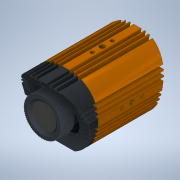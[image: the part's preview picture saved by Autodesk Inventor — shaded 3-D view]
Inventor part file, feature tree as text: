
AUTODESK INVENTOR PART (.ipt)
format: ipt  version: 2022 (Build 260153000, 153)  size: 11,512,320 bytes
history: native  units: mm
features: sketch x28, extrude x16, plane x8, hole x8, projected_geometry x6, other x3, chamfer x2, split x1, helix x1, pattern_circular x1, mirror x1
ambient origin geometry x8: Origin, YZ Plane, XZ Plane, XY Plane, X Axis, Y Axis, Z Axis, Center Point
bodies: Solid1 (feature_tree), Solid2 (feature_tree), Solid3 (feature_tree)
feature tree (75):
  extrude  "Extrusion1"  Depth=62.28mm
  extrude  "Extrusion2"  Depth=9.388mm
  sketch  "Sketch3"  dims[d5=18.0mm d6=31.8mm]
  plane  "Work Plane2"
  extrude  "Extrusion3"  Depth=31.8mm
  extrude  "Extrusion4"  Depth=14.0mm
  extrude  "Extrusion5"  Depth=94.6mm TaperAngle=0.0deg
  chamfer  "Chamfer1"  Distance=1.6mm Angle=90.0deg
  extrude  "Extrusion6"  Depth=94.6mm TaperAngle=0.0deg
  chamfer  "Chamfer2"  Distance=9.72mm
  hole  "Hole1"  [1 undecoded]
  hole  "Hole2"  [1 undecoded]
  hole  "Hole3"  [1 undecoded]
  hole  "Hole4"  [1 undecoded]
  hole  "Hole5"  [1 undecoded]
  hole  "Hole6"  [1 undecoded]
  hole  "Hole7"  [1 undecoded]
  hole  "Hole8"  [1 undecoded]
  plane  "Work Plane4"
  plane  "Work Plane5"
  plane  "Work Plane6"
  extrude  "Extrusion9"  Depth=8.0mm
  extrude  "Extrusion10"  Depth=40.0mm
  extrude  "Extrusion11"  Depth=32.5mm
  extrude  "Extrusion12"  Depth=25.0mm
  extrude  "Extrusion13"  Depth=32.5mm
  extrude  "Extrusion14"  Depth=10.0mm
  extrude  "Extrusion15"  Depth=4.3mm TaperAngle=0.0deg
  extrude  "Extrusion16"  TaperAngle=90.0deg  [1 undecoded]
  extrude  "Extrusion17"  Depth=10.0mm TaperAngle=0.0deg
  extrude  "Extrusion18"  Depth=50.8mm
  sketch  "Sketch30"  dims[d95=32.5mm]
  split  "Split1"
  helix  "Coil1"  [1 undecoded]
  pattern_circular  "Circular Pattern1"  [2 undecoded]
  plane  "Work Plane9"
  mirror  "Mirror1"
  plane  "Work Plane10"
  sketch  "Sketch35"  dims[d104=4.978mm d105=8.7mm d106=4.0mm d107=2.0mm d108=90.0deg d109=9.05mm d110=20.594885mm d111=4.3mm d119=0.0mm d125=90.0deg d132=10.0mm d133=0.0mm d135=50.8mm d136=6.97mm d137=4.86mm d139=7.7mm d140=3.15mm d141=3.15mm d142=1.12mm d143=1.12mm d144=3.15mm d145=1.12mm d146=3.15mm d147=3.15mm d148=1.12mm d149=3.15mm d151=7.7mm d152=3.15mm d153=1.12mm d154=3.15mm d155=1.12mm d156=3.15mm d157=3.15mm d158=1.12mm d159=3.15mm d160=1.12mm d161=3.15mm d162=10.0mm d163=0.0mm d164=13.86mm d165=0.0mm d166=0.8mm d167=1.6mm d168=2.27mm d169=0.0mm d172=0.82mm d173=0.3mm d175=0.3mm d176=0.3mm d177=0.3mm d178=0.3mm d179=0.3mm d180=0.3mm d181=0.3mm d182=0.3mm d183=0.3mm d184=0.3mm d185=0.3mm d188=5.0mm d189=0.0mm d190=0.82mm d191=0.3mm d192=0.3mm d193=0.3mm d194=0.3mm d195=0.3mm d196=0.3mm d197=0.3mm d198=0.3mm d199=0.3mm d200=0.3mm d201=0.3mm d202=0.3mm d203=6.0mm d204=0.0mm d220=13.7mm d221=3.32mm d222=1.0mm d223=1.0mm d224=0.0mm d225=0.3mm d226=0.5mm d227=5.0mm d228=0.7mm d229=0.5mm d230=0.2mm d231=1.0mm d232=0.0mm d233=0.5mm d234=6.0mm d235=0.5mm d236=1.0mm d237=0.0mm d238=1.3mm d239=1.3mm d240=1.5mm d241=0.0mm d243=1.0mm d244=135.0deg d245=0.5mm d246=10.0mm d247=14.0mm d248=1.0mm d249=0.0mm d250=90.0deg d251=90.0deg d252=0.0mm d253=0.0mm d254=720.0mm d255=360.0deg d257=-7.0mm d261=370.0mm]
  sketch  "Sketch1"  dims[d0=64.76mm d1=62.28mm]
  sketch  "Sketch2"  dims[d2=94.6mm d3=0.0mm d4=9.388mm]
  plane  "Work Plane1"
  sketch  "Sketch4"  dims[d7=31.8mm d8=14.0mm]
  sketch  "Sketch5"  dims[d9=7.388mm d10=94.6mm d11=0.0mm]
  sketch  "Sketch6"  dims[d12=70.0mm d13=90.0deg d14=1.6mm]
  sketch  "Sketch7"  dims[d15=44.7mm d16=94.6mm d17=0.0mm]
  sketch  "Sketch9"  dims[d18=30.0mm d19=9.72mm d20=0.0mm]
  sketch  "Sketch10"  dims[d21=36.92mm d22=13.25mm d23=0.0mm]
  projected_geometry  "Projected Loop1"
  sketch  "Sketch11"  dims[d24=3.46mm d25=2.0mm d26=45.0deg d27=23.7mm]
  sketch  "Sketch12"  dims[d28=1.7mm d29=0.0mm d31=1.7mm d32=2.0mm d33=60.0deg]
  sketch  "Sketch13"  dims[d34=31.8mm d35=31.8mm]
  sketch  "Sketch14"  dims[d36=22.0mm d37=20.0mm]
  sketch  "Sketch15"  dims[d38=3.459mm d39=8.0mm d40=4.0mm d41=2.0mm d42=90.0deg d43=9.8mm d44=20.594885mm d45=10.0mm]
  sketch  "Sketch16"  dims[d47=4.978mm d48=8.7mm d49=4.0mm d50=2.0mm d51=90.0deg d52=9.08mm d53=20.594885mm]
  plane  "Work Plane3"
  sketch  "Sketch20"  dims[d54=3.459mm d55=8.0mm d56=4.0mm d57=2.0mm d58=90.0deg d59=9.8mm d60=20.594885mm]
  projected_geometry  "Projected Loop3"
  sketch  "Sketch21"  dims[d61=4.978mm d62=12.7mm d63=4.0mm d64=2.0mm d65=90.0deg d66=19.05mm d67=20.594885mm d68=26.5mm]
  sketch  "Sketch22"  dims[d69=26.5mm d70=12.0mm]
  projected_geometry  "Projected Loop4"
  sketch  "Sketch23"  dims[d71=12.0mm d72=8.0mm]
  projected_geometry  "Projected Loop5"
  sketch  "Sketch24"  dims[d73=8.0mm d74=40.0mm]
  sketch  "Sketch25"  dims[d75=40.0mm]
  sketch  "Sketch26"  dims[d76=3.459mm d77=8.0mm d78=4.0mm d79=2.0mm d80=90.0deg d81=9.8mm d82=20.594885mm d83=32.5mm]
  sketch  "Sketch27"  dims[d84=20.0mm]
  projected_geometry  "Projected Loop6"
  sketch  "Sketch28"  dims[d85=4.978mm d86=9.0mm d87=4.0mm d88=2.0mm d89=90.0deg d90=9.05mm d91=20.594885mm d92=25.0mm]
  sketch  "Sketch29"  dims[d93=20.0mm d94=32.5mm]
  sketch  "Sketch33"  dims[d96=3.459mm d97=8.0mm d98=4.0mm d99=2.0mm d100=90.0deg d101=9.8mm d102=20.594885mm d103=10.0mm]
  projected_geometry  "Projected Loop7"
  other  "<userpath>\Documents\Inventor\AM Research\Assembly2.iam"
  other  "Assembly2.iam"
  other  "Part1:1"
note: 12 required parameter values undecoded (feature->parameter linkage not recoverable at this tier; creation-order binding heuristic only, values carry confidence <= 0.55)
